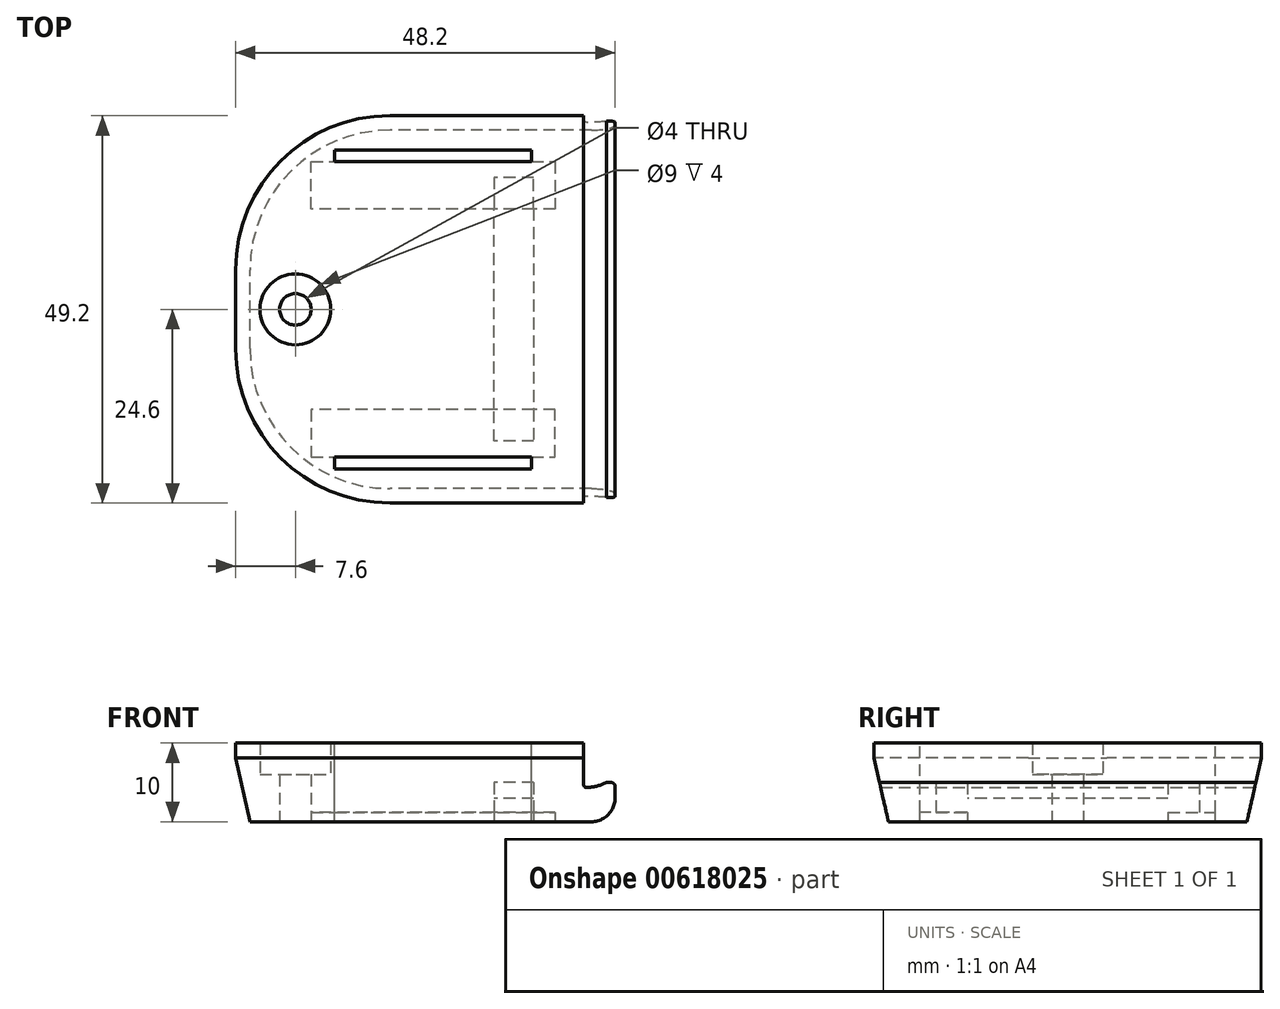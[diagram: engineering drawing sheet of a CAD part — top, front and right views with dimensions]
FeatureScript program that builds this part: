
annotation { "Feature Type Name" : "Feature", "Feature Type Description" : "" }
export const myFeature = defineFeature(function(context is Context, id is Id, definition is map)
    precondition{}
    {
        {
            var Q0;
            Q0=qCreatedBy(makeId("Top.planeOp"),FACE);
            var sketch = newSketch(context, id + "F0", { "sketchPlane" : qUnion([Q0])});
            skLineSegment(sketch, "E0", {"start": v(29.38, 0) * mm, "end": v(-30.29, 0) * mm, "construction": true});
            skLineSegment(sketch, "E1", {"start": v(30, 24.95) * mm, "end": v(30, -24) * mm, "construction": true});
            skLineSegment(sketch, "E2", {"start": v(30, 19.5) * mm, "end": v(5, 19.5) * mm, "construction": true});
            skLineSegment(sketch, "E3", {"start": v(30, -19.5) * mm, "end": v(5, -19.5) * mm, "construction": true});
            skLineSegment(sketch, "E4.bottom", {"start": v(37, 25) * mm, "end": v(12, 25) * mm});
            skLineSegment(sketch, "E4.top", {"start": v(37, -25) * mm, "end": v(12, -25) * mm});
            skLineSegment(sketch, "E4.left", {"start": v(37, 25) * mm, "end": v(37, -25) * mm});
            skLineSegment(sketch, "E4.right", {"start": v(-8, 5) * mm, "end": v(-8, -5) * mm});
            skPoint(sketch, "E5.visualSharp", {"position": v(-8, 25) * mm});
            skArc(sketch, "E5.filletArc", {"start": v(12, 25) * mm, "mid": v(-2.14, 19.14) * mm, "end": v(-8, 5) * mm});
            skPoint(sketch, "E6.visualSharp", {"position": v(-8, -25) * mm});
            skArc(sketch, "E6.filletArc", {"start": v(-8, -5) * mm, "mid": v(-2.14, -19.14) * mm, "end": v(12, -25) * mm});
            skPoint(sketch, "E7", {"position": v(0, 0) * mm});
            skLineSegment(sketch, "E8.0", {"start": v(36.6, 24.6) * mm, "end": v(36.6, -24.6) * mm});
            skArc(sketch, "E8.1", {"start": v(12, 24.6) * mm, "mid": v(-1.86, 18.86) * mm, "end": v(-7.6, 5) * mm});
            skLineSegment(sketch, "E8.2", {"start": v(-7.6, 5) * mm, "end": v(-7.6, -5) * mm});
            skLineSegment(sketch, "E8.3", {"start": v(36.6, 24.6) * mm, "end": v(12, 24.6) * mm});
            skArc(sketch, "E8.4", {"start": v(-7.6, -5) * mm, "mid": v(-1.86, -18.86) * mm, "end": v(12, -24.6) * mm});
            skLineSegment(sketch, "E8.5", {"start": v(36.6, -24.6) * mm, "end": v(12, -24.6) * mm});
            skLineSegment(sketch, "E9.bottom", {"start": v(30, 20.25) * mm, "end": v(5, 20.25) * mm});
            skLineSegment(sketch, "E9.top", {"start": v(30, 18.75) * mm, "end": v(5, 18.75) * mm});
            skLineSegment(sketch, "E9.left", {"start": v(30, 20.25) * mm, "end": v(30, 18.75) * mm});
            skLineSegment(sketch, "E9.right", {"start": v(5, 20.25) * mm, "end": v(5, 18.75) * mm});
            skPoint(sketch, "E9.middle", {"position": v(17.5, 19.5) * mm});
            skLineSegment(sketch, "E10.bottom", {"start": v(30, -18.75) * mm, "end": v(5, -18.75) * mm});
            skLineSegment(sketch, "E10.top", {"start": v(30, -20.25) * mm, "end": v(5, -20.25) * mm});
            skLineSegment(sketch, "E10.left", {"start": v(30, -18.75) * mm, "end": v(30, -20.25) * mm});
            skLineSegment(sketch, "E10.right", {"start": v(5, -18.75) * mm, "end": v(5, -20.25) * mm});
            skPoint(sketch, "E10.middle", {"position": v(17.5, -19.5) * mm});
            skSolve(sketch);
        }
        {
            var Q0;
            Q0=makeQuery(id+"F0.imprint","IMPRINT",FACE,{"disambiguationData":[TD([[makeQuery(id+"F0.imprint","IMPRINT",EDGE,{"derivedFrom":sQuery(id+"F0.wireOp",EDGE,"E8.0")}),-1.0]])]});
            extrude(context, id + "F1", {"entities" : qUnion([Q0]), "oppositeDirection" : true, "depth" : 10 * mm, "offsetDistance" : 25 * mm});
        }
        {
            var Q0;
            Q0=sQuery(id+"F0.wireOp",VERTEX,"E7");
            var Q1;
            Q1=makeQuery(id+"F1.opExtrude","SWEPT_BODY",BODY,{"disambiguationData":[OSD([sQuery(id+"F0.wireOp",EDGE,"E8.0"),sQuery(id+"F0.wireOp",EDGE,"E8.1"),sQuery(id+"F0.wireOp",EDGE,"E8.2"),sQuery(id+"F0.wireOp",EDGE,"E8.3"),sQuery(id+"F0.wireOp",EDGE,"E8.4"),sQuery(id+"F0.wireOp",EDGE,"E8.5"),sQuery(id+"F0.wireOp",EDGE,"E9.bottom"),sQuery(id+"F0.wireOp",EDGE,"E9.top"),sQuery(id+"F0.wireOp",EDGE,"E9.left"),sQuery(id+"F0.wireOp",EDGE,"E9.right"),sQuery(id+"F0.wireOp",EDGE,"E10.bottom"),sQuery(id+"F0.wireOp",EDGE,"E10.top"),sQuery(id+"F0.wireOp",EDGE,"E10.left"),sQuery(id+"F0.wireOp",EDGE,"E10.right")])]});
            hole(context, id + "F2", {"style" : HoleStyle.C_BORE, "endStyle" : HoleEndStyle.BLIND, "holeDiameter" : 4 * mm, "cBoreDiameter" : 9 * mm, "cBoreDepth" : 4 * mm, "majorDiameter" : 5 * mm, "holeDepth" : 12 * mm, "isTappedThrough" : true, "tappedDepth" : 12 * mm, "tapClearance" : 3, "locations" : qUnion([Q0]), "scope" : qUnion([Q1])});
        }
        {
            var Q0;
            Q0=makeQuery(id+"F1.opExtrude","CAP_FACE",FACE,{"disambiguationData":[OSD([sQuery(id+"F0.wireOp",EDGE,"E8.0"),sQuery(id+"F0.wireOp",EDGE,"E8.1"),sQuery(id+"F0.wireOp",EDGE,"E8.2"),sQuery(id+"F0.wireOp",EDGE,"E8.3"),sQuery(id+"F0.wireOp",EDGE,"E8.4"),sQuery(id+"F0.wireOp",EDGE,"E8.5"),sQuery(id+"F0.wireOp",EDGE,"E9.bottom"),sQuery(id+"F0.wireOp",EDGE,"E9.top"),sQuery(id+"F0.wireOp",EDGE,"E9.left"),sQuery(id+"F0.wireOp",EDGE,"E9.right"),sQuery(id+"F0.wireOp",EDGE,"E10.bottom"),sQuery(id+"F0.wireOp",EDGE,"E10.top"),sQuery(id+"F0.wireOp",EDGE,"E10.left"),sQuery(id+"F0.wireOp",EDGE,"E10.right")])],"isStart":false});
            var sketch = newSketch(context, id + "F3", { "sketchPlane" : qUnion([Q0])});
            skLineSegment(sketch, "E11", {"start": v(30, -18.75) * mm, "end": v(33, -18.75) * mm});
            skLineSegment(sketch, "E12", {"start": v(33, -18.75) * mm, "end": v(33, -12.75) * mm});
            skLineSegment(sketch, "E13", {"start": v(33, -12.75) * mm, "end": v(2, -12.75) * mm});
            skLineSegment(sketch, "E14", {"start": v(2, -12.75) * mm, "end": v(2, -18.75) * mm});
            skLineSegment(sketch, "E15", {"start": v(2, -18.75) * mm, "end": v(5, -18.75) * mm});
            skLineSegment(sketch, "E16.MirrorCS", {"start": v(30, 18.75) * mm, "end": v(33, 18.75) * mm});
            skLineSegment(sketch, "E17.MirrorCS", {"start": v(33, 18.75) * mm, "end": v(33, 12.75) * mm});
            skLineSegment(sketch, "E18.MirrorCS", {"start": v(33, 12.75) * mm, "end": v(2, 12.75) * mm});
            skLineSegment(sketch, "E19.MirrorCS", {"start": v(2, 12.75) * mm, "end": v(2, 18.75) * mm});
            skLineSegment(sketch, "E20.MirrorCS", {"start": v(2, 18.75) * mm, "end": v(5, 18.75) * mm});
            skLineSegment(sketch, "E21", {"start": v(30.26, -12.75) * mm, "end": v(30.26, -16.75) * mm});
            skLineSegment(sketch, "E22", {"start": v(30.26, -16.75) * mm, "end": v(25.26, -16.75) * mm});
            skLineSegment(sketch, "E23", {"start": v(25.26, -16.75) * mm, "end": v(25.26, -12.75) * mm});
            skLineSegment(sketch, "E24", {"start": v(30.26, -12.75) * mm, "end": v(30.26, 16.75) * mm});
            skLineSegment(sketch, "E25", {"start": v(30.26, 16.75) * mm, "end": v(25.26, 16.75) * mm});
            skLineSegment(sketch, "E26", {"start": v(25.26, 16.75) * mm, "end": v(25.26, -12.75) * mm});
            skSolve(sketch);
        }
        {
            var Q0;
            Q0=makeQuery(id+"F3.imprint","IMPRINT",FACE,{"disambiguationData":[TD([[makeQuery(id+"F3.imprint","IMPRINT",EDGE,{"derivedFrom":sQuery(id+"F3.wireOp",EDGE,"E11")}),1.0]])]});
            var Q1;
            Q1=makeQuery(id+"F3.imprint","IMPRINT",FACE,{"disambiguationData":[TD([[makeQuery(id+"F3.imprint","IMPRINT",EDGE,{"derivedFrom":sQuery(id+"F3.wireOp",EDGE,"E16.MirrorCS")}),-1.0]])]});
            extrude(context, id + "F4", {"entities" : qUnion([Q0, Q1]), "operationType" : NewBodyOperationType.REMOVE, "oppositeDirection" : true, "depth" : 1.2 * mm, "offsetDistance" : 25 * mm});
        }
        {
            var Q0;
            {var subQ0=sQuery(id+"F3.wireOp",EDGE,"E24");var subQ5=sQuery(id+"F3.wireOp",EDGE,"E18.MirrorCS");var subQ6=makeQuery(id+"F3.imprint","INTERSECT",VERTEX,{"derivedFrom":[subQ5,subQ0]});Q0=makeQuery(id+"F3.imprint","IMPRINT",FACE,{"disambiguationData":[TD([[makeQuery(id+"F3.imprint","IMPRINT",EDGE,{"disambiguationData":[TD([[subQ6,-1.0]])],"derivedFrom":subQ5}),1.0]])]});}
            var Q1;
            {var subQ0=sQuery(id+"F3.wireOp",EDGE,"E21");Q1=makeQuery(id+"F3.imprint","IMPRINT",FACE,{"disambiguationData":[TD([[makeQuery(id+"F3.imprint","IMPRINT",EDGE,{"derivedFrom":subQ0}),-1.0]])]});}
            var Q2;
            {var subQ5=sQuery(id+"F3.wireOp",EDGE,"E25");Q2=makeQuery(id+"F3.imprint","IMPRINT",FACE,{"disambiguationData":[TD([[makeQuery(id+"F3.imprint","IMPRINT",EDGE,{"derivedFrom":subQ5}),1.0]])]});}
            extrude(context, id + "F5", {"entities" : qUnion([Q0, Q1, Q2]), "operationType" : NewBodyOperationType.REMOVE, "oppositeDirection" : true, "depth" : 3 * mm, "offsetDistance" : 25 * mm});
        }
        {
            var Q0;
            {var subQ0=sQuery(id+"F3.wireOp",EDGE,"E21");Q0=makeQuery(id+"F3.imprint","IMPRINT",FACE,{"disambiguationData":[TD([[makeQuery(id+"F3.imprint","IMPRINT",EDGE,{"derivedFrom":subQ0}),-1.0]])]});}
            var Q1;
            {var subQ5=sQuery(id+"F3.wireOp",EDGE,"E25");Q1=makeQuery(id+"F3.imprint","IMPRINT",FACE,{"disambiguationData":[TD([[makeQuery(id+"F3.imprint","IMPRINT",EDGE,{"derivedFrom":subQ5}),1.0]])]});}
            extrude(context, id + "F6", {"entities" : qUnion([Q0, Q1]), "operationType" : NewBodyOperationType.REMOVE, "oppositeDirection" : true, "depth" : 5 * mm, "offsetDistance" : 25 * mm});
        }
        {
            var Q0;
            Q0=makeQuery(id+"F1.opExtrude","SWEPT_FACE",FACE,{"disambiguationData":[OSD([sQuery(id+"F0.wireOp",EDGE,"E8.0")])]});
            var sketch = newSketch(context, id + "F7", { "sketchPlane" : qUnion([Q0])});
            skLineSegment(sketch, "E27", {"start": v(24.6, -5) * mm, "end": v(-24.6, -5) * mm});
            skSolve(sketch);
        }
        {
            var Q0;
            {var subQ0=sQuery(id+"F7.wireOp",EDGE,"E27");Q0=makeQuery(id+"F7.imprint","IMPRINT",FACE,{"disambiguationData":[TD([[makeQuery(id+"F7.imprint","IMPRINT",EDGE,{"derivedFrom":subQ0}),1.0]])]});}
            extrude(context, id + "F8", {"entities" : qUnion([Q0]), "operationType" : NewBodyOperationType.ADD, "depth" : 4 * mm, "offsetDistance" : 25 * mm});
        }
        {
            var Q0;
            {var subQ0=sQuery(id+"F0.wireOp",EDGE,"E8.3");Q0=makeQuery(id+"F8.boolean.opBoolean","MERGE",FACE,{"derivedFrom":[makeQuery(id+"F1.opExtrude","SWEPT_FACE",FACE,{"disambiguationData":[OSD([subQ0])]}),makeQuery(id+"F8.opExtrude","SWEPT_FACE",FACE,{"disambiguationData":[OSD([sQuery(id+"F0.wireOp",EDGE,"E8.0"),subQ0])]})]});}
            var sketch = newSketch(context, id + "F9", { "sketchPlane" : qUnion([Q0])});
            skFitSpline(sketch, "E28", {"points": [v(-39.5, -5) * mm, v(-38.68, -5.35) * mm, v(-36.73, -5.55) * mm, v(-36.6, -5) * mm], "startDerivative": vector(2.03, -1.12) * mm, "endDerivative": vector(-0.27, 2.73) * mm});
            skSolve(sketch);
        }
        {
            var Q0;
            {var subQ0=sQuery(id+"F9.wireOp",EDGE,"E28");Q0=makeQuery(id+"F9.imprint","IMPRINT",FACE,{"disambiguationData":[TD([[makeQuery(id+"F9.imprint","IMPRINT",EDGE,{"derivedFrom":subQ0}),1.0]])]});}
            extrude(context, id + "F10", {"entities" : qUnion([Q0]), "operationType" : NewBodyOperationType.REMOVE, "oppositeDirection" : true, "depth" : 55 * mm, "offsetDistance" : 25 * mm});
        }
        {
            var Q0;
            Q0=makeQuery(id+"F8.opExtrude","CAP_EDGE",EDGE,{"disambiguationData":[OSD([sQuery(id+"F0.wireOp",EDGE,"E8.0")])],"isStart":false});
            fillet(context, id + "F11", {"entities" : qUnion([Q0]), "tangentPropagation" : true, "radius" : 3 * mm, "defaultsChanged" : true, "vertexSettings" : [], "allowEdgeOverflow" : false});
        }
        {
            var Q0;
            Q0=makeQuery(id+"F8.opExtrude","CAP_EDGE",EDGE,{"disambiguationData":[OSD([sQuery(id+"F7.wireOp",EDGE,"E27")])],"isStart":false});
            var Q1;
            {var subQ0=sQuery(id+"F9.wireOp",EDGE,"E28");var subQ1=sQuery(id+"F7.wireOp",EDGE,"E27");var subQ2=sQuery(id+"F0.wireOp",EDGE,"E8.3");var subQ3=sQuery(id+"F0.wireOp",EDGE,"E8.0");Q1=makeQuery(id+"F10.boolean.opBoolean","COPY",EDGE,{"derivedFrom":makeQuery(id+"F10.opExtrude","SWEPT_EDGE",EDGE,{"disambiguationData":[OSD([subQ3,subQ2,subQ1,subQ0]),TDD([makeQuery(id+"F9.imprint","INTERSECT",VERTEX,{"derivedFrom":[makeQuery(id+"F8.opExtrude","SWEPT_EDGE",EDGE,{"disambiguationData":[OSD([subQ3,subQ2,subQ1])]}),subQ0]})])]})});}
            fillet(context, id + "F12", {"entities" : qUnion([Q0, Q1]), "tangentPropagation" : true, "radius" : .5 * mm, "defaultsChanged" : false, "vertexSettings" : [], "allowEdgeOverflow" : false});
        }
        {
            var Q0;
            Q0=qCreatedBy(makeId("Front.planeOp"),FACE);
            var sketch = newSketch(context, id + "F13", { "sketchPlane" : qUnion([Q0])});
            skLineSegment(sketch, "E29", {"start": v(-8.02, 0) * mm, "end": v(-5.51, -11.14) * mm});
            skLineSegment(sketch, "E30", {"start": v(-5.51, -11.14) * mm, "end": v(-8.02, -11.14) * mm});
            skLineSegment(sketch, "E31", {"start": v(-8.02, -11.14) * mm, "end": v(-8.02, 0) * mm});
            skSolve(sketch);
        }
        {
            var Q0;
            Q0=makeQuery(id+"F13.imprint","IMPRINT",FACE,{"disambiguationData":[TD([[makeQuery(id+"F13.imprint","IMPRINT",EDGE,{"derivedFrom":sQuery(id+"F13.wireOp",EDGE,"E29")}),-1.0]])]});
            var Q1;
            Q1=makeQuery(id+"F1.opExtrude","CAP_EDGE",EDGE,{"disambiguationData":[OSD([sQuery(id+"F0.wireOp",EDGE,"E8.1")])],"isStart":false});
            var Q2;
            Q2=makeQuery(id+"F1.opExtrude","CAP_EDGE",EDGE,{"disambiguationData":[OSD([sQuery(id+"F0.wireOp",EDGE,"E8.2")])],"isStart":false});
            var Q3;
            Q3=makeQuery(id+"F1.opExtrude","CAP_EDGE",EDGE,{"disambiguationData":[OSD([sQuery(id+"F0.wireOp",EDGE,"E8.4")])],"isStart":false});
            sweep(context, id + "F14", {"operationType" : NewBodyOperationType.REMOVE, "profiles" : qUnion([Q0]), "path" : qUnion([Q1, Q2, Q3])});
        }
        {
            var Q0;
            Q0=makeQuery(id+"F14.boolean.opBoolean","COPY",FACE,{"derivedFrom":makeQuery(id+"F14.opSweep","CAP_FACE",FACE,{"disambiguationData":[OSD([sQuery(id+"F0.wireOp",EDGE,"E8.1"),sQuery(id+"F0.wireOp",EDGE,"E8.3"),sQuery(id+"F13.wireOp",EDGE,"E29"),sQuery(id+"F13.wireOp",EDGE,"E30"),sQuery(id+"F13.wireOp",EDGE,"E31")])],"isStart":true})});
            var Q1;
            Q1=makeQuery(id+"F14.boolean.opBoolean","COPY",FACE,{"derivedFrom":makeQuery(id+"F14.opSweep","CAP_FACE",FACE,{"disambiguationData":[OSD([sQuery(id+"F0.wireOp",EDGE,"E8.4"),sQuery(id+"F0.wireOp",EDGE,"E8.5"),sQuery(id+"F13.wireOp",EDGE,"E29"),sQuery(id+"F13.wireOp",EDGE,"E30"),sQuery(id+"F13.wireOp",EDGE,"E31")])],"isStart":false})});
            extrude(context, id + "F15", {"entities" : qUnion([Q0, Q1]), "operationType" : NewBodyOperationType.REMOVE, "oppositeDirection" : true, "depth" : 30 * mm, "offsetDistance" : 25 * mm});
        }
    });
